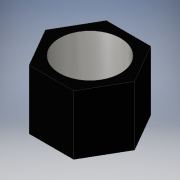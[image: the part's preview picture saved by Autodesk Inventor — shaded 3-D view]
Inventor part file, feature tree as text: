
AUTODESK INVENTOR PART (.ipt)
format: ipt  version: 2016 (Build 200138000, 138)  size: 100,864 bytes
history: native  units: in
note: dims shown in document units (in); Inventor stores cm internally (conversion verified against a paired STEP export)
features: extrude x1, sketch x1
ambient origin geometry x8: Origin, YZ Plane, XZ Plane, XY Plane, X Axis, Y Axis, Z Axis, Center Point
bodies: Solid1 (feature_tree)
feature tree (2):
  extrude  "Extrusion1"  Depth=0.1575in
  sketch  "Sketch1"  dims[d0=0.1181in d1=0.1614in d2=0.1575in d3=0.0in]
